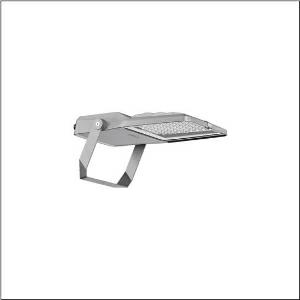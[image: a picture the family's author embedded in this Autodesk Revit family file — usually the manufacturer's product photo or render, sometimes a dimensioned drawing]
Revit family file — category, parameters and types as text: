
# Revit family: floodlight_fl_21_mini___pl43_5xa7771b2a1a_1af5
name_source: partatom
category: Lighting Fixtures
units: mm (PartAtom-declared; Revit-internal decimal feet)

## family parameters
Cut with Voids When Loaded = No
Host = Face
Light Source = No
Part Type = Normal
Room Calculation Point = No
Round Connector Dimension = Use Diameter
Shared = No

## types (1)
- --- (1 x LED, 6400 lm, 45.5 W, 3000K)
    Apparent Load = 46 VA
    CIE Flux Codes = 27 78 99 100 100
    Color Rendering = 70
    Color Temperature = 3000K
    Default Elevation = 1800 mm
    Description = Floodlight FL 21 mini, floodlight, primary light control with lens, of PMMA, primary optical cover: protective disc, of toughened safety glass, transparent, light distribution: PL43, light emission: direct distribution, installation type: surface-mounted, LED, High Power LED, rated luminous flux: 6.400lm, luminous efficacy: 141lm/W, light colour: 730, colour temperature: 3000K, control gear: ECG iQ, control: Auto-Match, Temp-Guard, Lumen-Switch, Night-Set, Smart-Wire, Light-Fading, Desk-Remote (wireless, voltage-free reading and setting of iQ features in the workshop via application-optimized NFC function/RFID function), optimised constant luminous flux control (CLO 2.0), with terminal, 6-pole, mains connection: 220..240V, AC, 50/60Hz, start of lifetime: 46W, end of lifetime: 48W, reduction: 22W, luminaire housing, of diecast aluminium, powder-coated, Siteco® metallic grey (DB 702S), corrosivity category C5 according to DIN EN ISO 12944, mounting bracket, of steel, galvanised, powder-coated, Siteco® metallic grey (DB 702S), protection rating (complete): IP66, insulation class (complete): insulation class II (safety insulation), certification: CE, ENEC, VDE, protection symbol: D, impact resistance: IK08, permissible operating ambient temperature: -40..+40°C, permissible operating ambient temperature for outdoor applications: -40..+50°C, standard: DIN EN 12944, packaging unit: 1 piece

Light Distribution: PL43
    Height = 70 mm
    Lamp = 1 x LED
    Lamp Light Flux = 6400 lm
    Lamp Power = 45.5 W
    Lamp count = 1
    Length = 485 mm
    Luminous efficacy = 141 lm/W
    Manufacturer = Siteco
    ModVariant = No
    Model = 5XA7771B2A1A
    Number of Poles = 1
    OnlyDefault = Yes
    Power Factor = 1
    Product Name = Floodlight FL 21 mini | PL43
    Product group = floodlight | pylon top
    ProductGroupID = 6101
    Protection Class = Protection class II
    Protection Degree = IP 66
    RLX_Detail_Level = 1
    RlxData = <blob elided: 96033 chars, md5=17014a17>
    Socket = socket
    Standby Power = 0 W
    System Light Flux = 6400 lm
    System Power = 46 W
    Type Comments = factory setting: luminous flux: 100 % | dim-lin: 254 | 463 mA
    Type Image = l_1006845.jpg
    URL = http://relux.com
    VarID = @adj_074265
    Voltage = 0 V
    Weight = 0.00 kg
    Width = 337 mm

## geometry (parser evidence)
native form markers: Blend x4, Sweep x11
no freeform markers — native parametric forms only
